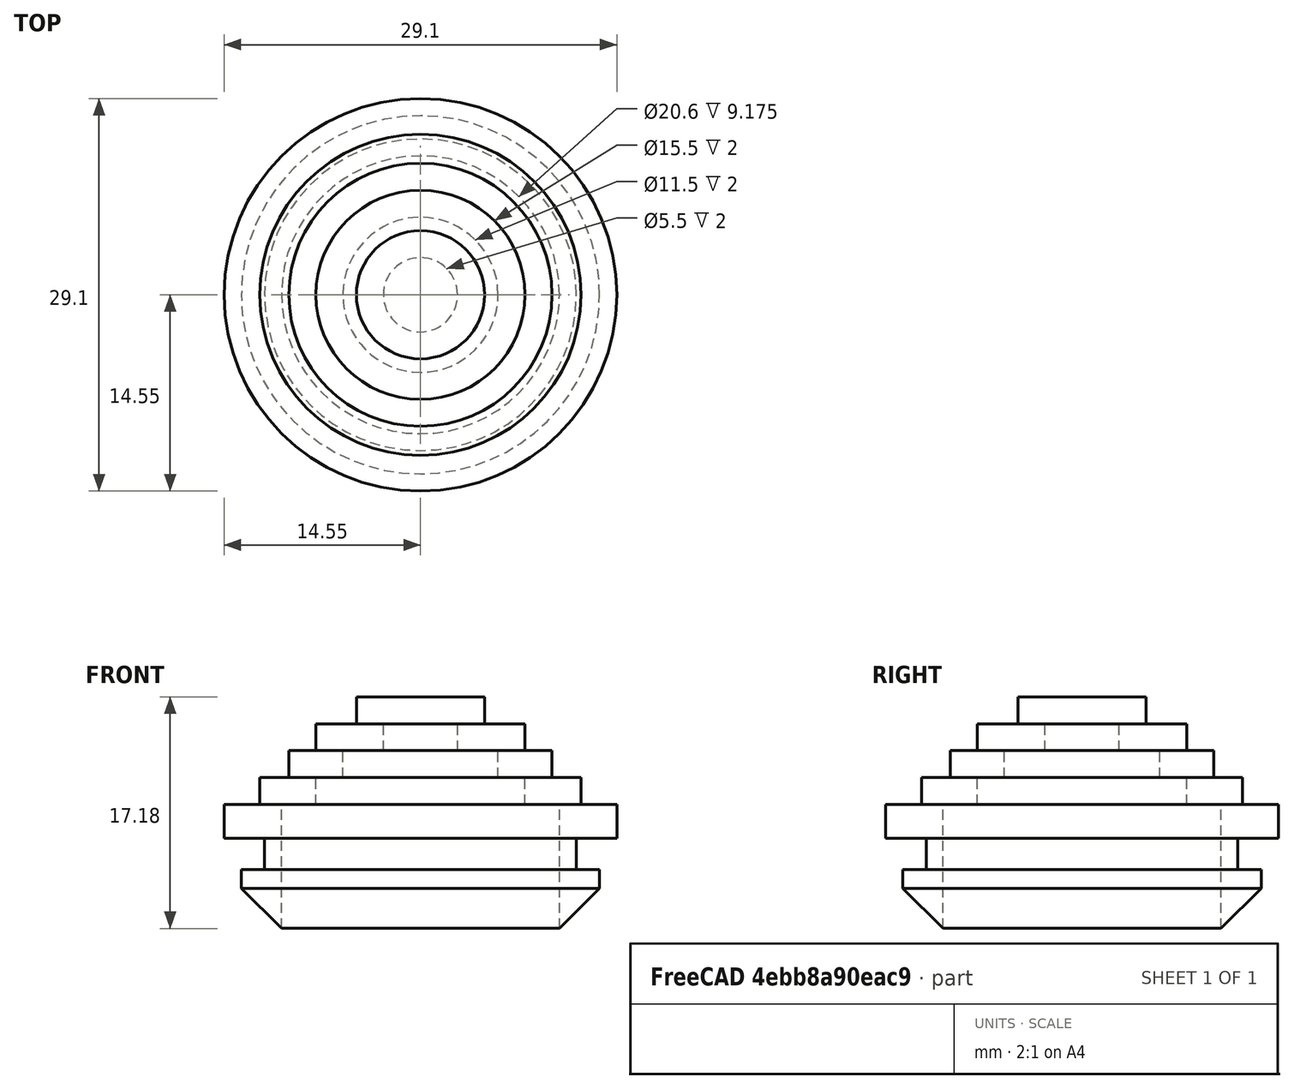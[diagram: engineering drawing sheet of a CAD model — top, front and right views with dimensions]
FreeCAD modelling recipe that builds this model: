
FCSTD DOCUMENT  (FreeCAD 0.22R36731 (Git))
Label: wire_holder
License: All rights reserved
LicenseURL: http://en.wikipedia.org/wiki/All_rights_reserved
objects: Sketcher::SketchObject×1, PartDesign::Revolution×1, PartDesign::CoordinateSystem×1, PartDesign::Body×1
note: 5 computed .brp shape members not serialized (recipe doc carries the construction recipe); baked Part::Feature solids carry a one-line shape summary decoded from their .brp

FEATURE [Sketcher::SketchObject] Sketch
  AttachmentSupport = -> [XZ_Plane]
  FullyConstrained = true
  MapMode = 5
  Placement = pos=(0,0,0) rot=(1,0,0;1.5708rad)
  sketch-geometry (25):
    g0: LineSegment StartX=14.55 StartY=0 StartZ=0 EndX=11.55 EndY=0 EndZ=0
    g1: LineSegment StartX=11.55 StartY=0 StartZ=0 EndX=11.55 EndY=-2.3 EndZ=0
    g2: LineSegment StartX=11.55 StartY=-2.3 StartZ=0 EndX=13.275 EndY=-2.3 EndZ=0
    g3: LineSegment StartX=10.3 StartY=-6.675 StartZ=0 EndX=10.3 EndY=2.5 EndZ=0
    g4: LineSegment StartX=10.3 StartY=2.5 StartZ=0 EndX=7.75 EndY=2.5 EndZ=0
    g5: LineSegment StartX=7.75 StartY=2.5 StartZ=0 EndX=7.75 EndY=4.5 EndZ=0
    g6: LineSegment StartX=7.75 StartY=4.5 StartZ=0 EndX=5.75 EndY=4.5 EndZ=0
    g7: LineSegment StartX=5.75 StartY=4.5 StartZ=0 EndX=5.75 EndY=6.5 EndZ=0
    g8: LineSegment StartX=5.75 StartY=6.5 StartZ=0 EndX=2.75 EndY=6.5 EndZ=0
    g9: LineSegment StartX=2.75 StartY=6.5 StartZ=0 EndX=2.75 EndY=8.5 EndZ=0
    g10: LineSegment StartX=2.75 StartY=8.5 StartZ=0 EndX=0 EndY=8.5 EndZ=0
    g11: LineSegment StartX=0 StartY=8.5 StartZ=0 EndX=0 EndY=10.5 EndZ=0
    g12: LineSegment StartX=0 StartY=10.5 StartZ=0 EndX=4.75 EndY=10.5 EndZ=0
    g13: LineSegment StartX=4.75 StartY=10.5 StartZ=0 EndX=4.75 EndY=8.5 EndZ=0
    g14: LineSegment StartX=4.75 StartY=8.5 StartZ=0 EndX=7.75 EndY=8.5 EndZ=0
    g15: LineSegment StartX=7.75 StartY=8.5 StartZ=0 EndX=7.75 EndY=6.5 EndZ=0
    g16: LineSegment StartX=7.75 StartY=6.5 StartZ=0 EndX=9.75 EndY=6.5 EndZ=0
    g17: LineSegment StartX=9.75 StartY=6.5 StartZ=0 EndX=9.75 EndY=4.5 EndZ=0
    g18: LineSegment StartX=9.75 StartY=4.5 StartZ=0 EndX=11.9 EndY=4.5 EndZ=0
    g19: LineSegment StartX=11.9 StartY=4.5 StartZ=0 EndX=11.9 EndY=2.5 EndZ=0
    g20: LineSegment StartX=11.9 StartY=2.5 StartZ=0 EndX=14.55 EndY=2.5 EndZ=0
    g21: LineSegment StartX=14.55 StartY=2.5 StartZ=0 EndX=14.55 EndY=0 EndZ=0
    g22: LineSegment StartX=13.275 StartY=-2.3 StartZ=0 EndX=13.275 EndY=-3.7 EndZ=0
    g23: LineSegment StartX=13.275 StartY=-3.7 StartZ=0 EndX=10.3 EndY=-6.675 EndZ=0
    g24: GeomPoint X=-11.55 Y=0 Z=0
  constraints (74):
    c: PointOnObject(g0,g-1)
    c: PointOnObject(g0,g-1)
    c: Coincident(g0,g1)
    c: Vertical(g1)
    c: Coincident(g1,g2)
    c: Coincident(g2,g22)
    c: Coincident(g23,g3)
    c: Vertical(g3)
    c: Coincident(g3,g4)
    c: Coincident(g4,g5)
    c: Coincident(g5,g6)
    c: Horizontal(g6)
    c: Coincident(g6,g7)
    c: Vertical(g7)
    c: Coincident(g7,g8)
    c: Horizontal(g8)
    c: Coincident(g8,g9)
    c: Vertical(g9)
    c: Coincident(g9,g10)
    c: Horizontal(g10)
    c: Coincident(g10,g11)
    c: PointOnObject(g11,g-2)
    c: Vertical(g11)
    c: Coincident(g11,g12)
    c: Horizontal(g12)
    c: Coincident(g12,g13)
    c: Vertical(g13)
    c: Coincident(g13,g14)
    c: Horizontal(g14)
    c: Coincident(g14,g15)
    c: Vertical(g15)
    c: Coincident(g15,g16)
    c: Horizontal(g16)
    c: Coincident(g16,g17)
    c: Vertical(g17)
    c: Coincident(g17,g18)
    c: Horizontal(g18)
    c: Coincident(g18,g19)
    c: Coincident(g21,g0)
    c: Horizontal(g4)
    c: Vertical(g5)
    c: DistanceX(g12) = 4.75
    c: DistanceX(g14) = 7.75
    c: DistanceX(g16) = 9.75
    c: DistanceX(g18) = 11.9
    c: Coincident(g19,g20)
    c: Vertical(g19)
    c: Coincident(g20,g21)
    c: Vertical(g21)
    c: Horizontal(g20)
    c: DistanceX(g20) = 14.55
    c: DistanceY(g21,g21) = 2.5
    c: DistanceY(g19,g19) = 2
    c: DistanceY(g17,g17) = 2
    c: DistanceY(g15,g15) = 2
    c: DistanceY(g13,g13) = 2
    c: DistanceX(g0) = 11.55
    c: DistanceX(g2) = 13.275
    c: DistanceY(g1,g1) = 2.3
    c: Horizontal(g2)
    c: Coincident(g22,g23)
    c: Vertical(g22)
    c: DistanceY(g22,g22) = 1.4
    c: DistanceX(g3) = 10.3
    c: Angle(g23) = -2.35619
    c: DistanceY(g11,g11) = 2
    c: DistanceX(g9,g13) = 2
    c: DistanceX(g7,g15) = 2
    c: Horizontal(g7,g15)
    c: Horizontal(g5,g17)
    c: DistanceX(g5,g17) = 2
    c: Horizontal(g3,g19)
    c: Symmetric(g24,g0,g-2)
    c: DistanceX(g24,g0) = 23.1  'fix_d'
FEATURE [PartDesign::Revolution] Revolution
  Angle = 360
  Angle2 = 60
  Axis = (0,2e-16,1)
  Base = (0,0,0)
  Placement = pos=(0,0,0) rot=(1,0,0;1.5708rad)
  Profile = -> Sketch
  ReferenceAxis = -> Sketch [V_Axis]
  Reversed = true
  Suppressed = false
  Type = 0
FEATURE [PartDesign::CoordinateSystem] Local_CS
  AttacherType = Attacher::AttachEngine3D
  AttachmentSupport = -> [XY_Plane]
  MapMode = 5
FEATURE [PartDesign::Body] Body
  Group = -> [Sketch,Revolution,Local_CS]
  Origin = -> Origin
  Tip = -> Revolution
